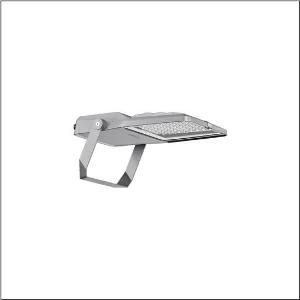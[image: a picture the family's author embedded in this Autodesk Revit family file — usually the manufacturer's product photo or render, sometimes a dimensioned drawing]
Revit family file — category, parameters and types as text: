
# Revit family: floodlight_fl_21_iq_mini___pl43_5xa7772c1a1a_56dc
name_source: partatom
category: Lighting Fixtures
units: mm (PartAtom-declared; Revit-internal decimal feet)

## family parameters
Cut with Voids When Loaded = No
Host = Face
Light Source = No
Part Type = Normal
Room Calculation Point = No
Round Connector Dimension = Use Diameter
Shared = No

## types (1)
- --- (1 x LED, 10370 lm, 87.2 W, 2200K)
    Apparent Load = 87 VA
    CIE Flux Codes = 27 78 99 100 100
    Color Rendering = 70
    Color Temperature = 2200K
    Default Elevation = 1800 mm
    Description = Floodlight FL 21 iQ mini, floodlight, primary light control with lens, of PMMA, primary optical cover: protective disc, of toughened safety glass, transparent, light distribution: PL43, light emission: direct distribution, installation type: surface-mounted, lamps: LED, High Power LED, rated values: 10.370lm | 87,2W | 118,9lm/W (begin service life); end service life: 10.370lm | 92,1W; at 50% lumin. flux: 5.185lm | 40,1W | 129,3lm/W, colour temperature: 2200K, colour rendering: CRI > 70, light colour: 722, light setting 1 begin service life: 100% | 10.370lm | 87,2W | 118,9lm/W | 2.200K, light setting 1 end service life: 92,1W, further light settings possible, control: Street-Remote, Auto-Match, Temp-Guard, Night-Set, Smart-Wire, Desk-Remote (wireless, voltage-free reading and setting of iQ features in the workshop via application-optimized NFC function/RFID function), optimised constant luminous flux control (CLO 2.0), pre-setting: linear dimming characteristic, with terminal, 6-pole, mains connection: 220..240V, AC, 50/60Hz, luminaire housing, of diecast aluminium, powder-coated, SITECO metallic grey (DB 702S), corrosivity category C5 mid according to DIN EN ISO 12944suitable for swimming poolschlorine-resistant, sealing non-destructively replaceable, mounting bracket, of steel, galvanised, powder-coated, SITECO metallic grey (DB 702S), protection rating (complete): IP66, insulation class (complete): insulation class II (safety insulation), certification: CE, ENEC, VDE, protection symbol: D, impact resistance: IK08, permissible operating ambient temperature: -40..+40°C, permissible operating ambient temperature for outdoor applications: -40..+50°C, standard: DIN EN 12944, LABS conformity tested according to VDMA 24364:2018-05, packaging unit: 1 piece

Light Distribution: PL43
    Height = 70 mm
    Lamp = 1 x LED
    Lamp Light Flux = 10370 lm
    Lamp Power = 87.2 W
    Lamp count = 1
    Length = 485 mm
    Luminous efficacy = 119 lm/W
    Manufacturer = Siteco
    ModVariant = No
    Model = 5XA7772C1A1A
    Mounting Place = Pole
    Mounting Type = Pole annexe
    Number of Poles = 1
    OnlyDefault = Yes
    Power Factor = 1
    Product Name = Floodlight FL 21 iQ mini | PL43
    Product group = floodlight | pylon annexe
    ProductGroupID = 6201
    Protection Class = Protection class II
    Protection Degree = IP 66
    RLX_Detail_Level = 1
    RLX_Emergency_Light_Flux = 0 lm
    RLX_Emergency_Type = 0
    RLX_Emergency_Type_DB = No
    RlxData = <blob elided: 96465 chars, md5=263a12d6>
    Socket = socket
    Standby Power = 0 W
    System Light Flux = 10370 lm
    System Power = 87 W
    Type Comments = factory setting: luminous flux: 100 % | dim-lin: 254 | 456 mA
    Type Image = l_1006845.jpg
    URL = http://relux.com
    VarID = @adj_163411
    Voltage = 0 V
    Weight = 0.00 kg
    Width = 337 mm

## geometry (parser evidence)
native form markers: Blend x4, Sweep x10
no freeform markers — native parametric forms only
